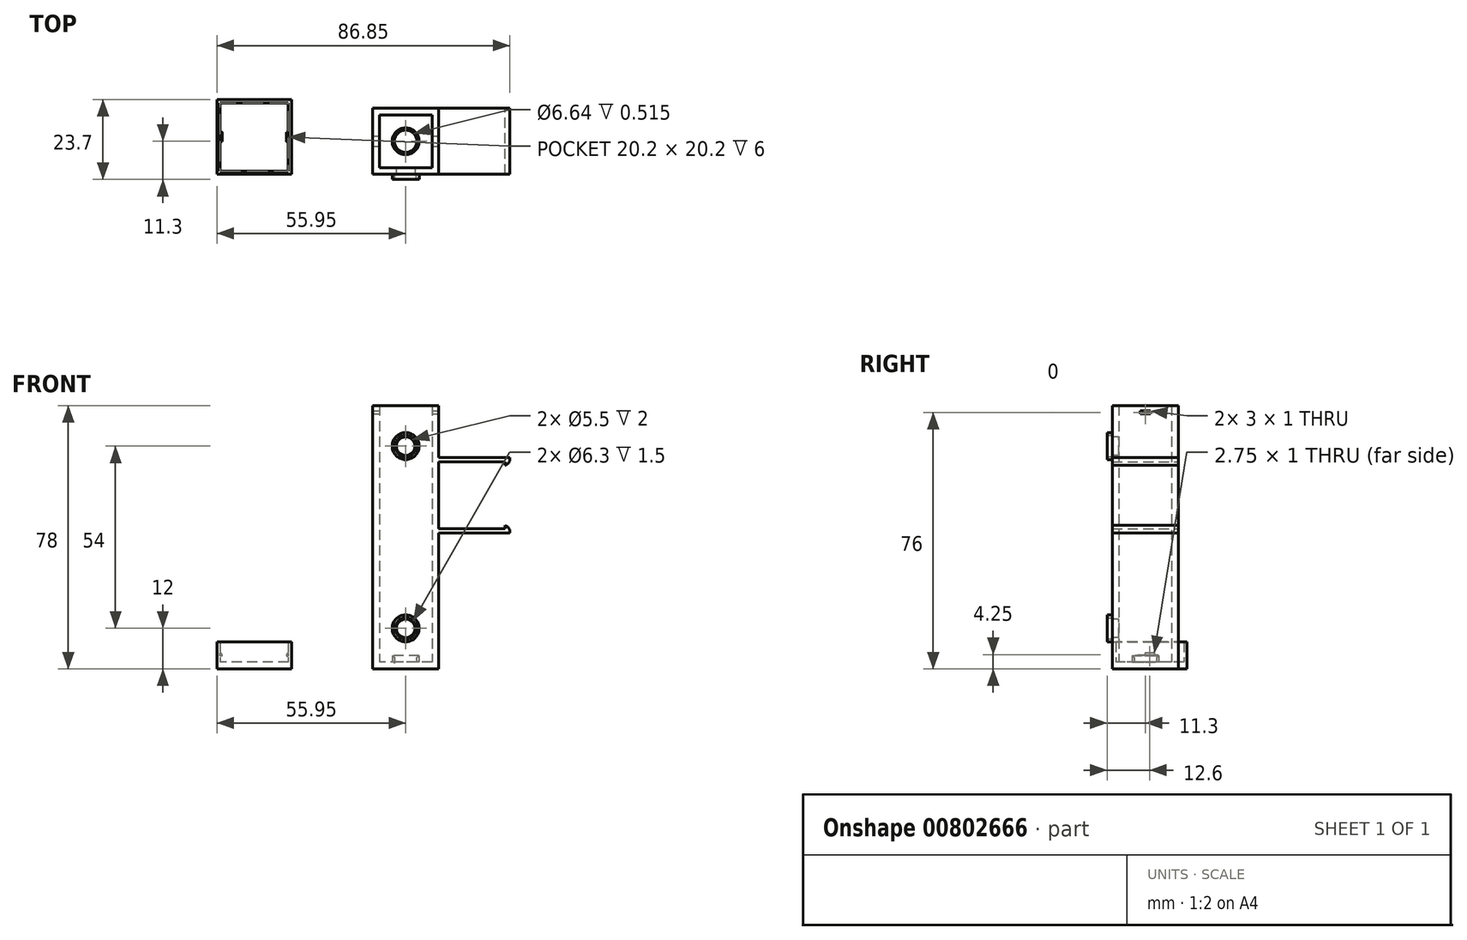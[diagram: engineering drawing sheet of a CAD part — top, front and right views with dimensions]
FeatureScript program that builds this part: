
annotation { "Feature Type Name" : "Feature", "Feature Type Description" : "" }
export const myFeature = defineFeature(function(context is Context, id is Id, definition is map)
    precondition{}
    {
        {
            var Q0;
            Q0=qCreatedBy(makeId("Top.planeOp"),FACE);
            var sketch = newSketch(context, id + "F0", { "sketchPlane" : qUnion([Q0])});
            skLineSegment(sketch, "E0.bottom", {"start": v(0, 0) * mm, "end": v(19.6, 0) * mm});
            skLineSegment(sketch, "E0.top", {"start": v(0, 19.6) * mm, "end": v(19.6, 19.6) * mm});
            skLineSegment(sketch, "E0.left", {"start": v(0, 0) * mm, "end": v(0, 19.6) * mm});
            skLineSegment(sketch, "E0.right", {"start": v(19.6, 0) * mm, "end": v(19.6, 19.6) * mm});
            skPoint(sketch, "E1", {"position": v(2, 2) * mm});
            skLineSegment(sketch, "E2.bottom", {"start": v(2, 2) * mm, "end": v(17.6, 2) * mm});
            skLineSegment(sketch, "E2.top", {"start": v(2, 17.6) * mm, "end": v(17.6, 17.6) * mm});
            skLineSegment(sketch, "E2.left", {"start": v(2, 2) * mm, "end": v(2, 17.6) * mm});
            skLineSegment(sketch, "E2.right", {"start": v(17.6, 2) * mm, "end": v(17.6, 17.6) * mm});
            skLineSegment(sketch, "E3.bottom", {"start": v(-23.95, 0) * mm, "end": v(-46.15, 0) * mm});
            skLineSegment(sketch, "E3.top", {"start": v(-23.95, 22.2) * mm, "end": v(-46.15, 22.2) * mm});
            skLineSegment(sketch, "E3.left", {"start": v(-23.95, 0) * mm, "end": v(-23.95, 22.2) * mm});
            skLineSegment(sketch, "E3.right", {"start": v(-46.15, 0) * mm, "end": v(-46.15, 22.2) * mm});
            skLineSegment(sketch, "E4", {"start": v(-35.05, 22.2) * mm, "end": v(-35.05, 0) * mm, "construction": true});
            skPoint(sketch, "E5", {"position": v(-24.45, 11.1) * mm});
            skPoint(sketch, "E5.positionSnap0", {"position": v(-23.95, 11.1) * mm});
            skPoint(sketch, "E6", {"position": v(-35.05, 11.1) * mm});
            skLineSegment(sketch, "E7.bottom", {"start": v(-25.05, 22.2) * mm, "end": v(-45.05, 22.2) * mm});
            skLineSegment(sketch, "E7.top", {"start": v(-25.05, 0) * mm, "end": v(-45.05, 0) * mm});
            skLineSegment(sketch, "E7.left", {"start": v(-25.05, 22.2) * mm, "end": v(-25.05, 0) * mm, "construction": true});
            skLineSegment(sketch, "E7.right", {"start": v(-45.05, 22.2) * mm, "end": v(-45.05, 0) * mm, "construction": true});
            skLineSegment(sketch, "E8.MirrorCS", {"start": v(-46.15, 12.47) * mm, "end": v(-46.15, 9.72) * mm});
            skLineSegment(sketch, "E9.bottom", {"start": v(-24.95, 21.2) * mm, "end": v(-45.15, 21.2) * mm});
            skLineSegment(sketch, "E9.top", {"start": v(-24.95, 1) * mm, "end": v(-45.15, 1) * mm});
            skLineSegment(sketch, "E9.left", {"start": v(-24.95, 21.2) * mm, "end": v(-24.95, 1) * mm});
            skLineSegment(sketch, "E9.right", {"start": v(-45.15, 21.2) * mm, "end": v(-45.15, 1) * mm});
            skPoint(sketch, "E10", {"position": v(9.8, 9.8) * mm});
            skPoint(sketch, "E10.positionSnap0", {"position": v(9.8, 17.6) * mm});
            skPoint(sketch, "E10.positionSnap1", {"position": v(2, 9.8) * mm});
            skCircle(sketch, "E11", {"center": v(9.8, 9.8) * mm, "radius": 6 * mm, "construction": true});
            skCircle(sketch, "E12", {"center": v(9.8, 9.8) * mm, "radius": 3.32 * mm});
            skCircle(sketch, "E13", {"center": v(9.8, 9.8) * mm, "radius": 3.97 * mm});
            skSolve(sketch);
        }
        {
            var Q0;
            Q0=makeQuery(id+"F0.imprint","IMPRINT",FACE,{"disambiguationData":[TD([[makeQuery(id+"F0.imprint","IMPRINT",EDGE,{"derivedFrom":sQuery(id+"F0.wireOp",EDGE,"E0.bottom")}),1.0]])]});
            var Q1;
            Q1=makeQuery(id+"F0.imprint","IMPRINT",FACE,{"disambiguationData":[TD([[makeQuery(id+"F0.imprint","IMPRINT",EDGE,{"derivedFrom":sQuery(id+"F0.wireOp",EDGE,"E2.bottom")}),1.0]])]});
            var Q2;
            Q2=makeQuery(id+"F0.imprint","IMPRINT",FACE,{"disambiguationData":[TD([[makeQuery(id+"F0.imprint","IMPRINT",EDGE,{"derivedFrom":sQuery(id+"F0.wireOp",EDGE,"E12")}),1.0]])]});
            extrude(context, id + "F1", {"entities" : qUnion([Q0, Q1, Q2]), "depth" : 2 * mm, "offsetDistance" : 25 * mm});
        }
        {
            var Q0;
            Q0=makeQuery(id+"F0.imprint","IMPRINT",FACE,{"disambiguationData":[TD([[makeQuery(id+"F0.imprint","IMPRINT",EDGE,{"derivedFrom":sQuery(id+"F0.wireOp",EDGE,"E0.bottom")}),1.0]])]});
            extrude(context, id + "F2", {"entities" : qUnion([Q0]), "operationType" : NewBodyOperationType.ADD, "depth" : 78 * mm, "offsetDistance" : 25 * mm});
        }
        {
            var Q0;
            {var subQ0=sQuery(id+"F0.wireOp",EDGE,"E0.bottom");Q0=makeQuery(id+"F2.boolean.opBoolean","MERGE",FACE,{"derivedFrom":[makeQuery(id+"F1.opExtrude","SWEPT_FACE",FACE,{"disambiguationData":[OSD([subQ0])]}),makeQuery(id+"F2.opExtrude","SWEPT_FACE",FACE,{"disambiguationData":[OSD([subQ0])]})]});}
            var sketch = newSketch(context, id + "F3", { "sketchPlane" : qUnion([Q0])});
            skPoint(sketch, "E14", {"position": v(9.8, 12) * mm});
            skPoint(sketch, "E14.positionSnap0", {"position": v(9.8, 0) * mm});
            skPoint(sketch, "E15", {"position": v(9.8, 66) * mm});
            skPoint(sketch, "E15.positionSnap0", {"position": v(9.8, 78) * mm});
            skCircle(sketch, "E16", {"center": v(9.8, 66) * mm, "radius": 3.15 * mm});
            skCircle(sketch, "E17", {"center": v(9.8, 66) * mm, "radius": 4 * mm});
            skCircle(sketch, "E18", {"center": v(9.8, 66) * mm, "radius": 2.75 * mm});
            skCircle(sketch, "E19", {"center": v(9.8, 12) * mm, "radius": 2.75 * mm});
            skCircle(sketch, "E20", {"center": v(9.8, 12) * mm, "radius": 3.15 * mm});
            skCircle(sketch, "E21", {"center": v(9.8, 12) * mm, "radius": 4 * mm});
            skPoint(sketch, "E22", {"position": v(9.8, 8) * mm});
            skCircle(sketch, "E23", {"center": v(9.8, 8) * mm, "radius": 6 * mm, "construction": true});
            skPoint(sketch, "E24", {"position": v(9.8, 2) * mm});
            skLineSegment(sketch, "E25", {"start": v(6.48, 3) * mm, "end": v(6.48, 0) * mm, "construction": true});
            skLineSegment(sketch, "E26", {"start": v(5.83, 0) * mm, "end": v(5.83, 3.5) * mm, "construction": true});
            skSolve(sketch);
        }
        {
            var Q0;
            Q0=makeQuery(id+"F3.imprint","IMPRINT",FACE,{"disambiguationData":[TD([[makeQuery(id+"F3.imprint","IMPRINT",EDGE,{"derivedFrom":sQuery(id+"F3.wireOp",EDGE,"E18")}),1.0]])]});
            var Q1;
            Q1=makeQuery(id+"F3.imprint","IMPRINT",FACE,{"disambiguationData":[TD([[makeQuery(id+"F3.imprint","IMPRINT",EDGE,{"derivedFrom":sQuery(id+"F3.wireOp",EDGE,"E19")}),1.0]])]});
            extrude(context, id + "F4", {"entities" : qUnion([Q0, Q1]), "operationType" : NewBodyOperationType.REMOVE, "oppositeDirection" : true, "depth" : 2 * mm, "offsetDistance" : 25 * mm});
        }
        {
            var Q0;
            {var subQ0=sQuery(id+"F0.wireOp",EDGE,"E0.right");Q0=makeQuery(id+"F2.boolean.opBoolean","MERGE",FACE,{"derivedFrom":[makeQuery(id+"F1.opExtrude","SWEPT_FACE",FACE,{"disambiguationData":[OSD([subQ0])]}),makeQuery(id+"F2.opExtrude","SWEPT_FACE",FACE,{"disambiguationData":[OSD([subQ0])]})]});}
            var sketch = newSketch(context, id + "F5", { "sketchPlane" : qUnion([Q0])});
            skPoint(sketch, "E27", {"position": v(0, 40.25) * mm});
            skLineSegment(sketch, "E28.bottom", {"start": v(0, 40.25) * mm, "end": v(19.6, 40.25) * mm});
            skLineSegment(sketch, "E28.top", {"start": v(0, 41.5) * mm, "end": v(19.6, 41.5) * mm});
            skLineSegment(sketch, "E28.left", {"start": v(0, 40.25) * mm, "end": v(0, 41.5) * mm});
            skLineSegment(sketch, "E28.right", {"start": v(19.6, 40.25) * mm, "end": v(19.6, 41.5) * mm});
            skPoint(sketch, "E29", {"position": v(0, 51.4) * mm});
            skLineSegment(sketch, "E30", {"start": v(0, 51.4) * mm, "end": v(19.6, 51.4) * mm});
            skPoint(sketch, "E31.MirrorP", {"position": v(0, 62.55) * mm});
            skLineSegment(sketch, "E32.MirrorCS", {"start": v(0, 62.55) * mm, "end": v(19.6, 62.55) * mm});
            skLineSegment(sketch, "E33.MirrorCS", {"start": v(0, 62.55) * mm, "end": v(0, 61.3) * mm});
            skLineSegment(sketch, "E34.MirrorCS", {"start": v(19.6, 62.55) * mm, "end": v(19.6, 61.3) * mm});
            skLineSegment(sketch, "E35.MirrorCS", {"start": v(0, 61.3) * mm, "end": v(19.6, 61.3) * mm});
            skSolve(sketch);
        }
        {
            var Q0;
            Q0=makeQuery(id+"F5.imprint","IMPRINT",FACE,{"disambiguationData":[TD([[makeQuery(id+"F5.imprint","IMPRINT",EDGE,{"derivedFrom":sQuery(id+"F5.wireOp",EDGE,"E28.bottom")}),1.0]])]});
            var Q1;
            Q1=makeQuery(id+"F5.imprint","IMPRINT",FACE,{"disambiguationData":[TD([[makeQuery(id+"F5.imprint","IMPRINT",EDGE,{"derivedFrom":sQuery(id+"F5.wireOp",EDGE,"E32.MirrorCS")}),-1.0]])]});
            extrude(context, id + "F6", {"entities" : qUnion([Q0, Q1]), "operationType" : NewBodyOperationType.ADD, "depth" : 21.1 * mm, "offsetDistance" : 25 * mm});
        }
        {
            var Q0;
            Q0=makeQuery(id+"F6.opExtrude","SWEPT_FACE",FACE,{"disambiguationData":[OSD([sQuery(id+"F5.wireOp",EDGE,"E28.top")])]});
            var sketch = newSketch(context, id + "F7", { "sketchPlane" : qUnion([Q0])});
            skLineSegment(sketch, "E36.bottom", {"start": v(40.7, 0) * mm, "end": v(39.2, 0) * mm});
            skLineSegment(sketch, "E36.top", {"start": v(40.7, 19.6) * mm, "end": v(39.2, 19.6) * mm});
            skLineSegment(sketch, "E36.left", {"start": v(40.7, 0) * mm, "end": v(40.7, 19.6) * mm});
            skLineSegment(sketch, "E36.right", {"start": v(39.2, 0) * mm, "end": v(39.2, 19.6) * mm});
            skSolve(sketch);
        }
        {
            var Q0;
            Q0=makeQuery(id+"F7.imprint","IMPRINT",FACE,{"disambiguationData":[TD([[makeQuery(id+"F7.imprint","IMPRINT",EDGE,{"derivedFrom":sQuery(id+"F7.wireOp",EDGE,"E36.bottom")}),-1.0]])]});
            extrude(context, id + "F8", {"entities" : qUnion([Q0]), "operationType" : NewBodyOperationType.ADD, "depth" : 1 * mm, "offsetDistance" : 25 * mm});
        }
        {
            var Q0;
            Q0=makeQuery(id+"F8.opExtrude","CAP_EDGE",EDGE,{"disambiguationData":[OSD([sQuery(id+"F7.wireOp",EDGE,"E36.left")])],"isStart":false});
            fillet(context, id + "F9", {"entities" : qUnion([Q0]), "radius" : 2 * mm, "tangentPropagation" : true, "allowEdgeOverflow" : false});
        }
        {
            var Q0;
            Q0=makeQuery(id+"F6.opExtrude","SWEPT_FACE",FACE,{"disambiguationData":[OSD([sQuery(id+"F5.wireOp",EDGE,"E35.MirrorCS")])]});
            var sketch = newSketch(context, id + "F10", { "sketchPlane" : qUnion([Q0])});
            skLineSegment(sketch, "E37.bottom", {"start": v(40.7, -19.6) * mm, "end": v(39.2, -19.6) * mm});
            skLineSegment(sketch, "E37.top", {"start": v(40.7, 0) * mm, "end": v(39.2, 0) * mm});
            skLineSegment(sketch, "E37.left", {"start": v(40.7, -19.6) * mm, "end": v(40.7, 0) * mm});
            skLineSegment(sketch, "E37.right", {"start": v(39.2, -19.6) * mm, "end": v(39.2, 0) * mm});
            skSolve(sketch);
        }
        {
            var Q0;
            Q0=makeQuery(id+"F10.imprint","IMPRINT",FACE,{"disambiguationData":[TD([[makeQuery(id+"F10.imprint","IMPRINT",EDGE,{"derivedFrom":sQuery(id+"F10.wireOp",EDGE,"E37.bottom")}),-1.0]])]});
            extrude(context, id + "F11", {"entities" : qUnion([Q0]), "operationType" : NewBodyOperationType.ADD, "depth" : 1 * mm, "offsetDistance" : 25 * mm});
        }
        {
            var Q0;
            Q0=makeQuery(id+"F11.opExtrude","CAP_EDGE",EDGE,{"disambiguationData":[OSD([sQuery(id+"F10.wireOp",EDGE,"E37.left")])],"isStart":false});
            fillet(context, id + "F12", {"entities" : qUnion([Q0]), "radius" : 2 * mm, "tangentPropagation" : true, "allowEdgeOverflow" : false});
        }
        {
            var Q0;
            {var subQ1=sQuery(id+"F0.wireOp",EDGE,"E0.right");Q0=makeQuery(id+"F6.boolean.opBoolean","SPLIT",FACE,{"disambiguationData":[TD([makeQuery(id+"F6.opExtrude","SWEPT_FACE",FACE,{"disambiguationData":[OSD([sQuery(id+"F5.wireOp",EDGE,"E32.MirrorCS")])]})])],"derivedFrom":makeQuery(id+"F2.boolean.opBoolean","MERGE",FACE,{"derivedFrom":[makeQuery(id+"F1.opExtrude","SWEPT_FACE",FACE,{"disambiguationData":[OSD([subQ1])]}),makeQuery(id+"F2.opExtrude","SWEPT_FACE",FACE,{"disambiguationData":[OSD([subQ1])]})]})});}
            var sketch = newSketch(context, id + "F13", { "sketchPlane" : qUnion([Q0])});
            skPoint(sketch, "E38", {"position": v(9.8, 76) * mm});
            skPoint(sketch, "E38.positionSnap0", {"position": v(9.8, 78) * mm});
            skLineSegment(sketch, "E39.bottom", {"start": v(8.3, 75.5) * mm, "end": v(11.3, 75.5) * mm});
            skLineSegment(sketch, "E39.top", {"start": v(8.3, 76.5) * mm, "end": v(11.3, 76.5) * mm});
            skLineSegment(sketch, "E39.left", {"start": v(8.3, 75.5) * mm, "end": v(8.3, 76.5) * mm});
            skLineSegment(sketch, "E39.right", {"start": v(11.3, 75.5) * mm, "end": v(11.3, 76.5) * mm});
            skSolve(sketch);
        }
        {
            var Q0;
            Q0=makeQuery(id+"F13.imprint","IMPRINT",FACE,{"disambiguationData":[TD([[makeQuery(id+"F13.imprint","IMPRINT",EDGE,{"derivedFrom":sQuery(id+"F13.wireOp",EDGE,"E39.bottom")}),1.0]])]});
            extrude(context, id + "F14", {"entities" : qUnion([Q0]), "operationType" : NewBodyOperationType.REMOVE, "oppositeDirection" : true, "depth" : 25 * mm, "offsetDistance" : 25 * mm});
        }
        {
            var Q0;
            {var subQ3=sQuery(id+"F0.wireOp",EDGE,"E3.left");Q0=makeQuery(id+"F0.imprint","IMPRINT",FACE,{"disambiguationData":[TD([[makeQuery(id+"F0.imprint","IMPRINT",EDGE,{"derivedFrom":subQ3}),1.0]])]});}
            extrude(context, id + "F15", {"entities" : qUnion([Q0]), "operationType" : NewBodyOperationType.ADD, "depth" : 8 * mm, "offsetDistance" : 25 * mm});
        }
        {
            var Q0;
            Q0=makeQuery(id+"F0.imprint","IMPRINT",FACE,{"disambiguationData":[TD([[makeQuery(id+"F0.imprint","IMPRINT",EDGE,{"derivedFrom":sQuery(id+"F0.wireOp",EDGE,"E9.bottom")}),1.0]])]});
            extrude(context, id + "F16", {"entities" : qUnion([Q0]), "operationType" : NewBodyOperationType.ADD, "depth" : 2 * mm, "offsetDistance" : 25 * mm});
        }
        {
            var Q0;
            Q0=makeQuery(id+"F15.opExtrude","SWEPT_FACE",FACE,{"disambiguationData":[OSD([sQuery(id+"F0.wireOp",EDGE,"E9.left")])]});
            var sketch = newSketch(context, id + "F17", { "sketchPlane" : qUnion([Q0])});
            skPoint(sketch, "E40", {"position": v(-11.1, 4.25) * mm});
            skPoint(sketch, "E40.positionSnap0", {"position": v(-11.1, 2) * mm});
            skLineSegment(sketch, "E41.bottom", {"start": v(-12.47, 4.75) * mm, "end": v(-9.72, 4.75) * mm});
            skLineSegment(sketch, "E41.top", {"start": v(-12.47, 3.75) * mm, "end": v(-9.72, 3.75) * mm});
            skLineSegment(sketch, "E41.left", {"start": v(-12.47, 4.75) * mm, "end": v(-12.47, 3.75) * mm});
            skLineSegment(sketch, "E41.right", {"start": v(-9.72, 4.75) * mm, "end": v(-9.72, 3.75) * mm});
            skSolve(sketch);
        }
        {
            var Q0;
            Q0=makeQuery(id+"F17.imprint","IMPRINT",FACE,{"disambiguationData":[TD([[makeQuery(id+"F17.imprint","IMPRINT",EDGE,{"derivedFrom":sQuery(id+"F17.wireOp",EDGE,"E41.bottom")}),-1.0]])]});
            extrude(context, id + "F18", {"entities" : qUnion([Q0]), "operationType" : NewBodyOperationType.ADD, "depth" : .6 * mm, "offsetDistance" : 25 * mm});
        }
        {
            var Q0;
            Q0=makeQuery(id+"F15.opExtrude","SWEPT_FACE",FACE,{"disambiguationData":[OSD([sQuery(id+"F0.wireOp",EDGE,"E9.right")])]});
            var sketch = newSketch(context, id + "F19", { "sketchPlane" : qUnion([Q0])});
            skPoint(sketch, "E42", {"position": v(11.1, 4.25) * mm});
            skPoint(sketch, "E42.positionSnap0", {"position": v(11.1, 2) * mm});
            skLineSegment(sketch, "E43.bottom", {"start": v(12.47, 3.75) * mm, "end": v(9.72, 3.75) * mm});
            skLineSegment(sketch, "E43.top", {"start": v(12.47, 4.75) * mm, "end": v(9.72, 4.75) * mm});
            skLineSegment(sketch, "E43.left", {"start": v(12.47, 3.75) * mm, "end": v(12.47, 4.75) * mm});
            skLineSegment(sketch, "E43.right", {"start": v(9.72, 3.75) * mm, "end": v(9.72, 4.75) * mm});
            skSolve(sketch);
        }
        {
            var Q0;
            Q0=makeQuery(id+"F19.imprint","IMPRINT",FACE,{"disambiguationData":[TD([[makeQuery(id+"F19.imprint","IMPRINT",EDGE,{"derivedFrom":sQuery(id+"F19.wireOp",EDGE,"E43.bottom")}),-1.0]])]});
            extrude(context, id + "F20", {"entities" : qUnion([Q0]), "operationType" : NewBodyOperationType.ADD, "depth" : .6 * mm, "offsetDistance" : 25 * mm});
        }
        {
            var Q0;
            Q0=makeQuery(id+"F18.opExtrude","CAP_EDGE",EDGE,{"disambiguationData":[OSD([sQuery(id+"F17.wireOp",EDGE,"E41.bottom")])],"isStart":false});
            var Q1;
            Q1=makeQuery(id+"F20.opExtrude","CAP_EDGE",EDGE,{"disambiguationData":[OSD([sQuery(id+"F19.wireOp",EDGE,"E43.top")])],"isStart":false});
            fillet(context, id + "F21", {"entities" : qUnion([Q0, Q1]), "radius" : 1 * mm, "tangentPropagation" : true, "allowEdgeOverflow" : false});
        }
        {
            var Q0;
            Q0=makeQuery(id+"F3.imprint","IMPRINT",FACE,{"disambiguationData":[TD([[makeQuery(id+"F3.imprint","IMPRINT",EDGE,{"derivedFrom":sQuery(id+"F3.wireOp",EDGE,"E18")}),1.0]])]});
            extrude(context, id + "F22", {"entities" : qUnion([Q0]), "operationType" : NewBodyOperationType.REMOVE, "oppositeDirection" : true, "depth" : 2 * mm, "offsetDistance" : 25 * mm});
        }
        {
            var Q0;
            Q0=makeQuery(id+"F3.imprint","IMPRINT",FACE,{"disambiguationData":[TD([[makeQuery(id+"F3.imprint","IMPRINT",EDGE,{"derivedFrom":sQuery(id+"F3.wireOp",EDGE,"E16")}),-1.0]])]});
            var Q1;
            Q1=makeQuery(id+"F3.imprint","IMPRINT",FACE,{"disambiguationData":[TD([[makeQuery(id+"F3.imprint","IMPRINT",EDGE,{"derivedFrom":sQuery(id+"F3.wireOp",EDGE,"E20")}),-1.0]])]});
            extrude(context, id + "F23", {"entities" : qUnion([Q0, Q1]), "operationType" : NewBodyOperationType.ADD, "depth" : 1.5 * mm, "offsetDistance" : 25 * mm});
        }
        {
            var Q0;
            Q0=makeQuery(id+"F0.imprint","IMPRINT",FACE,{"disambiguationData":[TD([[makeQuery(id+"F0.imprint","IMPRINT",EDGE,{"derivedFrom":sQuery(id+"F0.wireOp",EDGE,"E12")}),-1.0]])]});
            extrude(context, id + "F24", {"entities" : qUnion([Q0]), "operationType" : NewBodyOperationType.ADD, "depth" : 3.9 * mm, "offsetDistance" : 25 * mm});
        }
        {
            var Q0;
            Q0=makeQuery(id+"F24.opExtrude","CAP_EDGE",EDGE,{"disambiguationData":[OSD([sQuery(id+"F0.wireOp",EDGE,"E12")])],"isStart":false});
            fillet(context, id + "F25", {"entities" : qUnion([Q0]), "radius" : 1.8 * mm, "rho" : .99, "crossSection" : FilletCrossSection.CONIC, "allowEdgeOverflow" : false});
        }
    });
